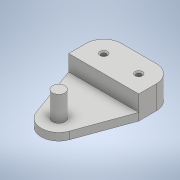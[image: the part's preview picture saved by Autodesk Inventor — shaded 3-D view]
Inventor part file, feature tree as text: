
AUTODESK INVENTOR PART (.ipt)
format: ipt  version: 2020 (Build 240168000, 168)  size: 142,848 bytes
history: native  units: mm
features: sketch x4, extrude x3, other x1, fillet x1, hole x1
ambient origin geometry x8: Origin, YZ Plane, XZ Plane, XY Plane, X Axis, Y Axis, Z Axis, Center Point
bodies: Body1 (feature_tree)
feature tree (10):
  other  "Твердое тело1"
  extrude  "Выдавливание1"  Depth=14.0mm
  extrude  "Выдавливание6"  Depth=7.0mm
  extrude  "Выдавливание9"  Depth=9.0mm
  fillet  "Сопряжение1"  Radius=3.5mm
  hole  "Отверстие1"  [1 undecoded]
  sketch  "Эскиз1"
  sketch  "Эскиз2"
  sketch  "Эскиз4"
  sketch  "Эскиз5"
note: 1 required parameter value undecoded (feature->parameter linkage not recoverable at this tier; creation-order binding heuristic only, values carry confidence <= 0.55)
